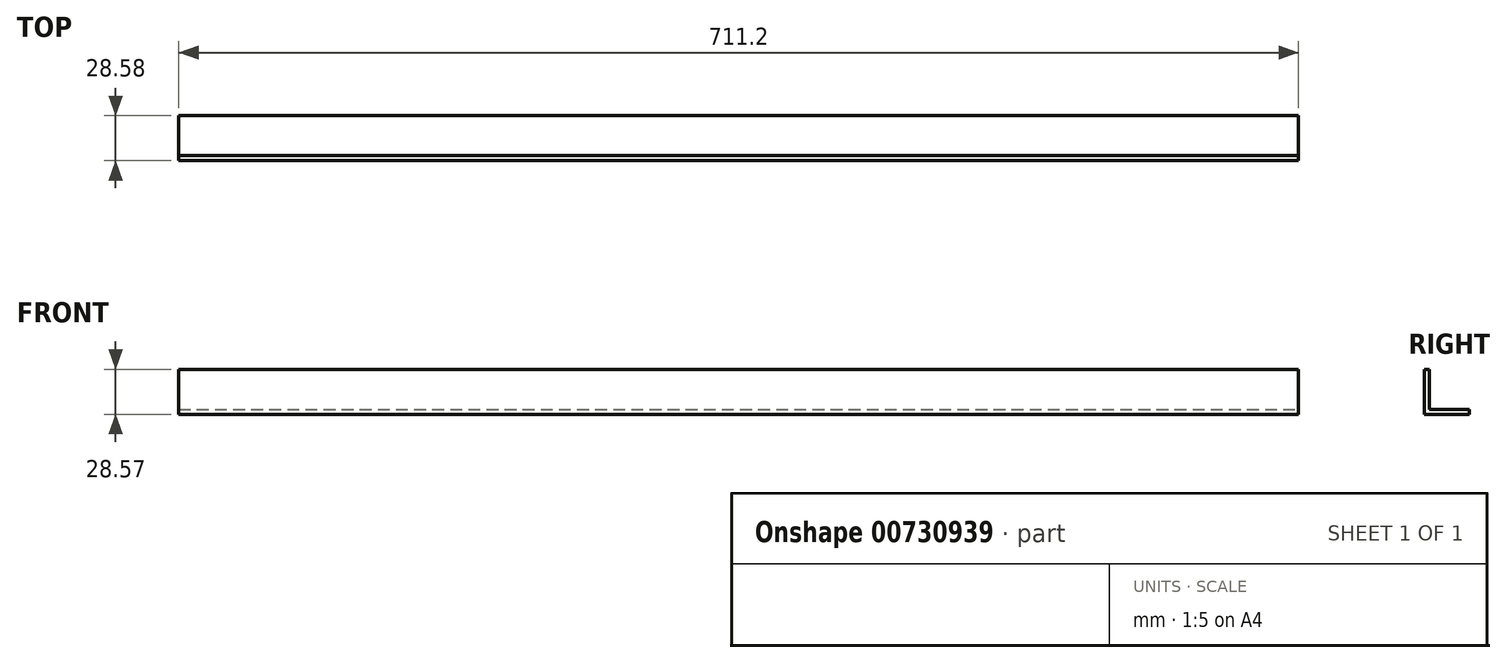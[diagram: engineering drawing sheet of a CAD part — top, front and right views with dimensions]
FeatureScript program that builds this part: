
annotation { "Feature Type Name" : "Feature", "Feature Type Description" : "" }
export const myFeature = defineFeature(function(context is Context, id is Id, definition is map)
    precondition{}
    {
        {
            var Q0;
            Q0=qCreatedBy(makeId("Right.planeOp"),FACE);
            var sketch = newSketch(context, id + "F0", { "sketchPlane" : qUnion([Q0])});
            skLineSegment(sketch, "E0", {"start": v(0, 0) * mm, "end": v(0, -25.4) * mm});
            skLineSegment(sketch, "E1", {"start": v(0, -25.4) * mm, "end": v(25.4, -25.4) * mm});
            skLineSegment(sketch, "E2.0", {"start": v(-3.17, -28.57) * mm, "end": v(25.4, -28.57) * mm});
            skLineSegment(sketch, "E2.1", {"start": v(-3.18, 0) * mm, "end": v(-3.17, -28.58) * mm});
            skLineSegment(sketch, "E3", {"start": v(-3.18, 0) * mm, "end": v(0, 0) * mm});
            skLineSegment(sketch, "E4", {"start": v(25.4, -25.4) * mm, "end": v(25.4, -28.57) * mm});
            skSolve(sketch);
        }
        {
            var Q0;
            Q0=makeQuery(id+"F0.imprint","IMPRINT",FACE,{"disambiguationData":[TD([[makeQuery(id+"F0.imprint","IMPRINT",EDGE,{"derivedFrom":sQuery(id+"F0.wireOp",EDGE,"E0")}),-1.0]])]});
            extrude(context, id + "F1", {"entities" : qUnion([Q0]), "oppositeDirection" : true, "depth" : 711.2 * mm, "offsetDistance" : 25.4 * mm});
        }
    });
